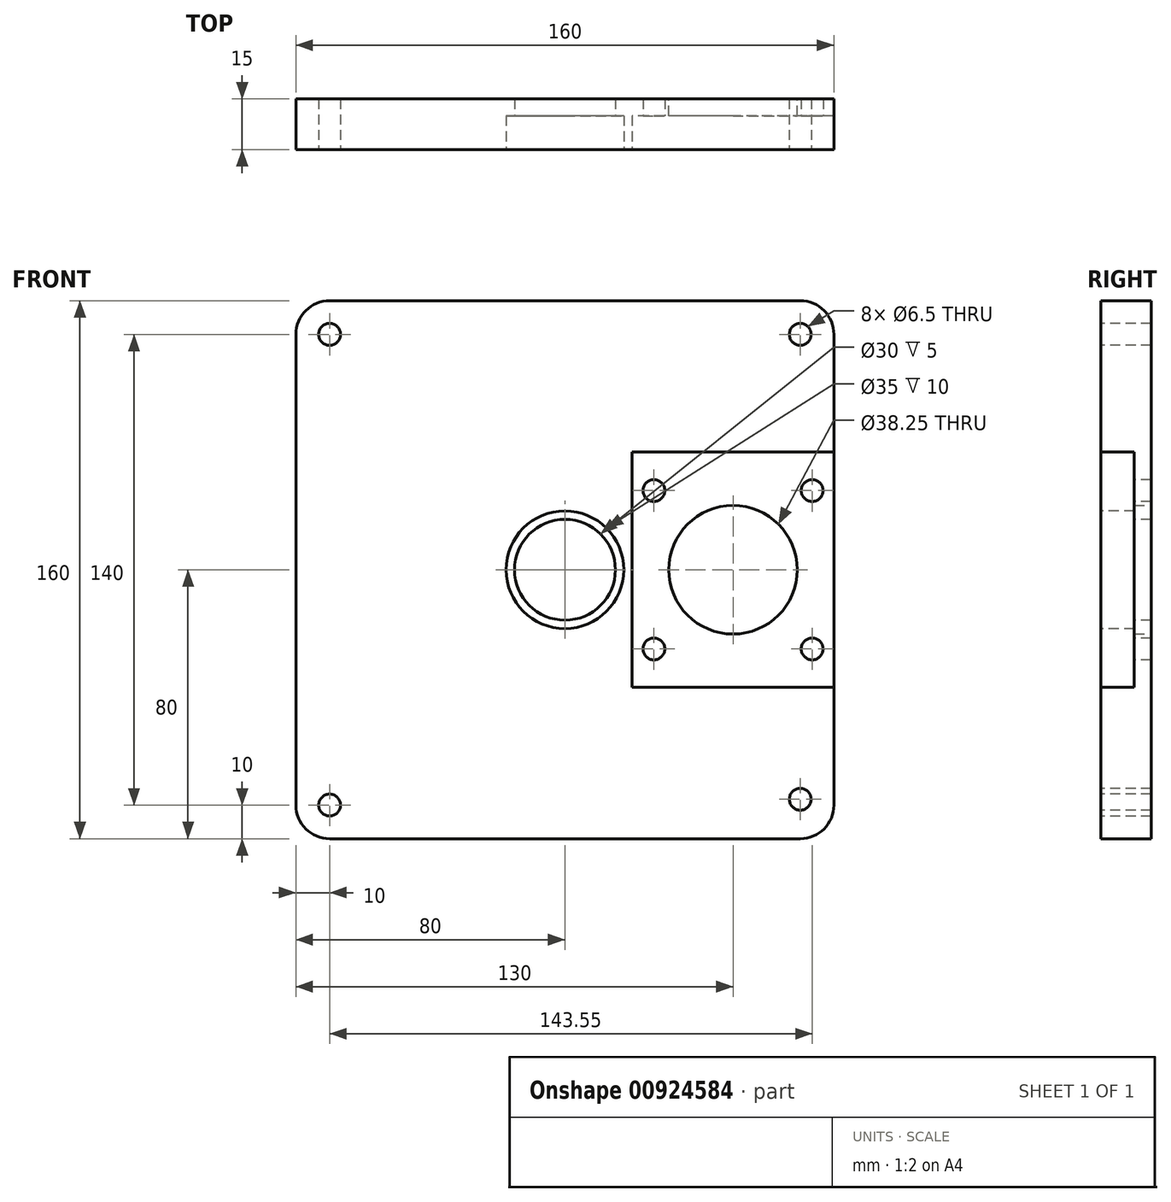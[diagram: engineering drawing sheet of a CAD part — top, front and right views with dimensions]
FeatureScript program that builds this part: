
annotation { "Feature Type Name" : "Feature", "Feature Type Description" : "" }
export const myFeature = defineFeature(function(context is Context, id is Id, definition is map)
    precondition{}
    {
        {
            var Q0;
            Q0=qCreatedBy(makeId("Front.planeOp"),FACE);
            var sketch = newSketch(context, id + "F0", { "sketchPlane" : qUnion([Q0])});
            skLineSegment(sketch, "E0.bottom", {"start": v(-80, 80) * mm, "end": v(80, 80) * mm});
            skLineSegment(sketch, "E0.top", {"start": v(-80, -80) * mm, "end": v(80, -80) * mm});
            skLineSegment(sketch, "E0.left", {"start": v(-80, 80) * mm, "end": v(-80, -80) * mm});
            skLineSegment(sketch, "E0.right", {"start": v(80, 80) * mm, "end": v(80, -80) * mm});
            skPoint(sketch, "E0.middle", {"position": v(0, 0) * mm});
            skSolve(sketch);
        }
        {
            var Q0;
            Q0=makeQuery(id+"F0.imprint","IMPRINT",FACE,{"disambiguationData":[TD([[makeQuery(id+"F0.imprint","IMPRINT",EDGE,{"derivedFrom":sQuery(id+"F0.wireOp",EDGE,"E0.bottom")}),-1.0]])]});
            extrude(context, id + "F1", {"entities" : qUnion([Q0]), "depth" : 15 * mm, "offsetDistance" : 25 * mm});
        }
        {
            var Q0;
            Q0=makeQuery(id+"F1.opExtrude","CAP_FACE",FACE,{"disambiguationData":[OSD([sQuery(id+"F0.wireOp",EDGE,"E0.bottom"),sQuery(id+"F0.wireOp",EDGE,"E0.top"),sQuery(id+"F0.wireOp",EDGE,"E0.left"),sQuery(id+"F0.wireOp",EDGE,"E0.right")])],"isStart":false});
            var sketch = newSketch(context, id + "F2", { "sketchPlane" : qUnion([Q0])});
            skCircle(sketch, "E1", {"center": v(0, 0) * mm, "radius": 15 * mm});
            skSolve(sketch);
        }
        {
            var Q0;
            Q0=makeQuery(id+"F2.imprint","IMPRINT",FACE,{"disambiguationData":[TD([[makeQuery(id+"F2.imprint","IMPRINT",EDGE,{"derivedFrom":sQuery(id+"F2.wireOp",EDGE,"E1")}),1.0]])]});
            extrude(context, id + "F3", {"entities" : qUnion([Q0]), "operationType" : NewBodyOperationType.REMOVE, "oppositeDirection" : true, "depth" : 25 * mm, "offsetDistance" : 25 * mm});
        }
        {
            var Q0;
            Q0=makeQuery(id+"F1.opExtrude","CAP_FACE",FACE,{"disambiguationData":[OSD([sQuery(id+"F0.wireOp",EDGE,"E0.bottom"),sQuery(id+"F0.wireOp",EDGE,"E0.top"),sQuery(id+"F0.wireOp",EDGE,"E0.left"),sQuery(id+"F0.wireOp",EDGE,"E0.right")])],"isStart":false});
            var sketch = newSketch(context, id + "F4", { "sketchPlane" : qUnion([Q0])});
            skCircle(sketch, "E2", {"center": v(0, 0) * mm, "radius": 17.5 * mm});
            skSolve(sketch);
        }
        {
            var Q0;
            Q0=makeQuery(id+"F4.imprint","IMPRINT",FACE,{"disambiguationData":[TD([[makeQuery(id+"F4.imprint","IMPRINT",EDGE,{"derivedFrom":sQuery(id+"F4.wireOp",EDGE,"E2")}),1.0]])]});
            extrude(context, id + "F5", {"entities" : qUnion([Q0]), "operationType" : NewBodyOperationType.REMOVE, "oppositeDirection" : true, "depth" : 10 * mm, "offsetDistance" : 25 * mm});
        }
        {
            var Q0;
            Q0=makeQuery(id+"F1.opExtrude","SWEPT_EDGE",EDGE,{"disambiguationData":[OSD([sQuery(id+"F0.wireOp",EDGE,"E0.bottom"),sQuery(id+"F0.wireOp",EDGE,"E0.right")])]});
            var Q1;
            Q1=makeQuery(id+"F1.opExtrude","SWEPT_EDGE",EDGE,{"disambiguationData":[OSD([sQuery(id+"F0.wireOp",EDGE,"E0.top"),sQuery(id+"F0.wireOp",EDGE,"E0.right")])]});
            var Q2;
            Q2=makeQuery(id+"F1.opExtrude","SWEPT_EDGE",EDGE,{"disambiguationData":[OSD([sQuery(id+"F0.wireOp",EDGE,"E0.top"),sQuery(id+"F0.wireOp",EDGE,"E0.left")])]});
            var Q3;
            Q3=makeQuery(id+"F1.opExtrude","SWEPT_EDGE",EDGE,{"disambiguationData":[OSD([sQuery(id+"F0.wireOp",EDGE,"E0.bottom"),sQuery(id+"F0.wireOp",EDGE,"E0.left")])]});
            fillet(context, id + "F6", {"entities" : qUnion([Q0, Q1, Q2, Q3]), "radius" : 10 * mm, "tangentPropagation" : true, "allowEdgeOverflow" : false});
        }
        {
            var Q0;
            Q0=makeQuery(id+"F1.opExtrude","CAP_FACE",FACE,{"disambiguationData":[OSD([sQuery(id+"F0.wireOp",EDGE,"E0.bottom"),sQuery(id+"F0.wireOp",EDGE,"E0.top"),sQuery(id+"F0.wireOp",EDGE,"E0.left"),sQuery(id+"F0.wireOp",EDGE,"E0.right")])],"isStart":false});
            var sketch = newSketch(context, id + "F7", { "sketchPlane" : qUnion([Q0])});
            skLineSegment(sketch, "E3.bottom", {"start": v(80, -35) * mm, "end": v(20, -35) * mm});
            skLineSegment(sketch, "E3.top", {"start": v(80, 35) * mm, "end": v(20, 35) * mm});
            skLineSegment(sketch, "E3.left", {"start": v(80, -35) * mm, "end": v(80, 35) * mm});
            skLineSegment(sketch, "E3.right", {"start": v(20, -35) * mm, "end": v(20, 35) * mm});
            skPoint(sketch, "E3.middle", {"position": v(50, 0) * mm});
            skSolve(sketch);
        }
        {
            var Q0;
            Q0=makeQuery(id+"F7.imprint","IMPRINT",FACE,{"disambiguationData":[TD([[makeQuery(id+"F7.imprint","IMPRINT",EDGE,{"derivedFrom":sQuery(id+"F7.wireOp",EDGE,"E3.bottom")}),-1.0]])]});
            extrude(context, id + "F8", {"entities" : qUnion([Q0]), "operationType" : NewBodyOperationType.REMOVE, "oppositeDirection" : true, "depth" : (10) * mm, "offsetDistance" : 25 * mm});
        }
        {
            var Q0;
            Q0=makeQuery(id+"F1.opExtrude","CAP_FACE",FACE,{"disambiguationData":[OSD([sQuery(id+"F0.wireOp",EDGE,"E0.bottom"),sQuery(id+"F0.wireOp",EDGE,"E0.top"),sQuery(id+"F0.wireOp",EDGE,"E0.left"),sQuery(id+"F0.wireOp",EDGE,"E0.right")])],"isStart":true});
            var sketch = newSketch(context, id + "F9", { "sketchPlane" : qUnion([Q0])});
            skCircle(sketch, "E4", {"center": v(-50, 0) * mm, "radius": 19.12 * mm});
            skSolve(sketch);
        }
        {
            var Q0;
            Q0=makeQuery(id+"F9.imprint","IMPRINT",FACE,{"disambiguationData":[TD([[makeQuery(id+"F9.imprint","IMPRINT",EDGE,{"derivedFrom":sQuery(id+"F9.wireOp",EDGE,"E4")}),1.0]])]});
            var Q1;
            Q1=sQuery(id+"F9.wireOp",EDGE,"E4");
            extrude(context, id + "F10", {"entities" : qUnion([Q0]), "operationType" : NewBodyOperationType.REMOVE, "surfaceEntities" : qUnion([Q1]), "oppositeDirection" : true, "depth" : 25 * mm, "offsetDistance" : 25 * mm});
        }
        {
            var Q0;
            Q0=makeQuery(id+"F8.boolean.opBoolean","COPY",FACE,{"derivedFrom":makeQuery(id+"F8.opExtrude","CAP_FACE",FACE,{"disambiguationData":[OSD([sQuery(id+"F7.wireOp",EDGE,"E3.bottom"),sQuery(id+"F7.wireOp",EDGE,"E3.top"),sQuery(id+"F7.wireOp",EDGE,"E3.left"),sQuery(id+"F7.wireOp",EDGE,"E3.right")])],"isStart":false})});
            var sketch = newSketch(context, id + "F11", { "sketchPlane" : qUnion([Q0])});
            skCircle(sketch, "E5", {"center": v(73.55, 23.55) * mm, "radius": 3.25 * mm});
            skCircle(sketch, "E6", {"center": v(26.45, 23.55) * mm, "radius": 3.25 * mm});
            skCircle(sketch, "E7", {"center": v(26.45, -23.55) * mm, "radius": 3.25 * mm});
            skCircle(sketch, "E8", {"center": v(73.55, -23.55) * mm, "radius": 3.25 * mm});
            skCircle(sketch, "E9.0", {"center": v(50, 0) * mm, "radius": 19.13 * mm});
            skSolve(sketch);
        }
        {
            var Q0;
            Q0=makeQuery(id+"F11.imprint","IMPRINT",FACE,{"disambiguationData":[TD([[makeQuery(id+"F11.imprint","IMPRINT",EDGE,{"derivedFrom":sQuery(id+"F11.wireOp",EDGE,"E6")}),1.0]])]});
            var Q1;
            Q1=makeQuery(id+"F11.imprint","IMPRINT",FACE,{"disambiguationData":[TD([[makeQuery(id+"F11.imprint","IMPRINT",EDGE,{"derivedFrom":sQuery(id+"F11.wireOp",EDGE,"E7")}),1.0]])]});
            var Q2;
            Q2=makeQuery(id+"F11.imprint","IMPRINT",FACE,{"disambiguationData":[TD([[makeQuery(id+"F11.imprint","IMPRINT",EDGE,{"derivedFrom":sQuery(id+"F11.wireOp",EDGE,"E8")}),1.0]])]});
            var Q3;
            Q3=makeQuery(id+"F11.imprint","IMPRINT",FACE,{"disambiguationData":[TD([[makeQuery(id+"F11.imprint","IMPRINT",EDGE,{"derivedFrom":sQuery(id+"F11.wireOp",EDGE,"E5")}),1.0]])]});
            extrude(context, id + "F12", {"entities" : qUnion([Q0, Q1, Q2, Q3]), "operationType" : NewBodyOperationType.REMOVE, "oppositeDirection" : true, "depth" : 25 * mm, "offsetDistance" : 25 * mm});
        }
        {
            var Q0;
            Q0=makeQuery(id+"F1.opExtrude","CAP_FACE",FACE,{"disambiguationData":[OSD([sQuery(id+"F0.wireOp",EDGE,"E0.bottom"),sQuery(id+"F0.wireOp",EDGE,"E0.top"),sQuery(id+"F0.wireOp",EDGE,"E0.left"),sQuery(id+"F0.wireOp",EDGE,"E0.right")])],"isStart":false});
            var sketch = newSketch(context, id + "F13", { "sketchPlane" : qUnion([Q0])});
            skCircle(sketch, "E10", {"center": v(70, 70) * mm, "radius": 3.25 * mm});
            skCircle(sketch, "E11", {"center": v(70, -68.26) * mm, "radius": 3.25 * mm});
            skCircle(sketch, "E12", {"center": v(-70, -70) * mm, "radius": 3.25 * mm});
            skCircle(sketch, "E13", {"center": v(-70, 70) * mm, "radius": 3.25 * mm});
            skSolve(sketch);
        }
        {
            var Q0;
            Q0=makeQuery(id+"F13.imprint","IMPRINT",FACE,{"disambiguationData":[TD([[makeQuery(id+"F13.imprint","IMPRINT",EDGE,{"derivedFrom":sQuery(id+"F13.wireOp",EDGE,"E10")}),1.0]])]});
            var Q1;
            Q1=makeQuery(id+"F13.imprint","IMPRINT",FACE,{"disambiguationData":[TD([[makeQuery(id+"F13.imprint","IMPRINT",EDGE,{"derivedFrom":sQuery(id+"F13.wireOp",EDGE,"E11")}),1.0]])]});
            var Q2;
            Q2=makeQuery(id+"F13.imprint","IMPRINT",FACE,{"disambiguationData":[TD([[makeQuery(id+"F13.imprint","IMPRINT",EDGE,{"derivedFrom":sQuery(id+"F13.wireOp",EDGE,"E12")}),1.0]])]});
            var Q3;
            Q3=makeQuery(id+"F13.imprint","IMPRINT",FACE,{"disambiguationData":[TD([[makeQuery(id+"F13.imprint","IMPRINT",EDGE,{"derivedFrom":sQuery(id+"F13.wireOp",EDGE,"E13")}),1.0]])]});
            extrude(context, id + "F14", {"entities" : qUnion([Q0, Q1, Q2, Q3]), "operationType" : NewBodyOperationType.REMOVE, "oppositeDirection" : true, "depth" : 25 * mm, "offsetDistance" : 25 * mm});
        }
    });
